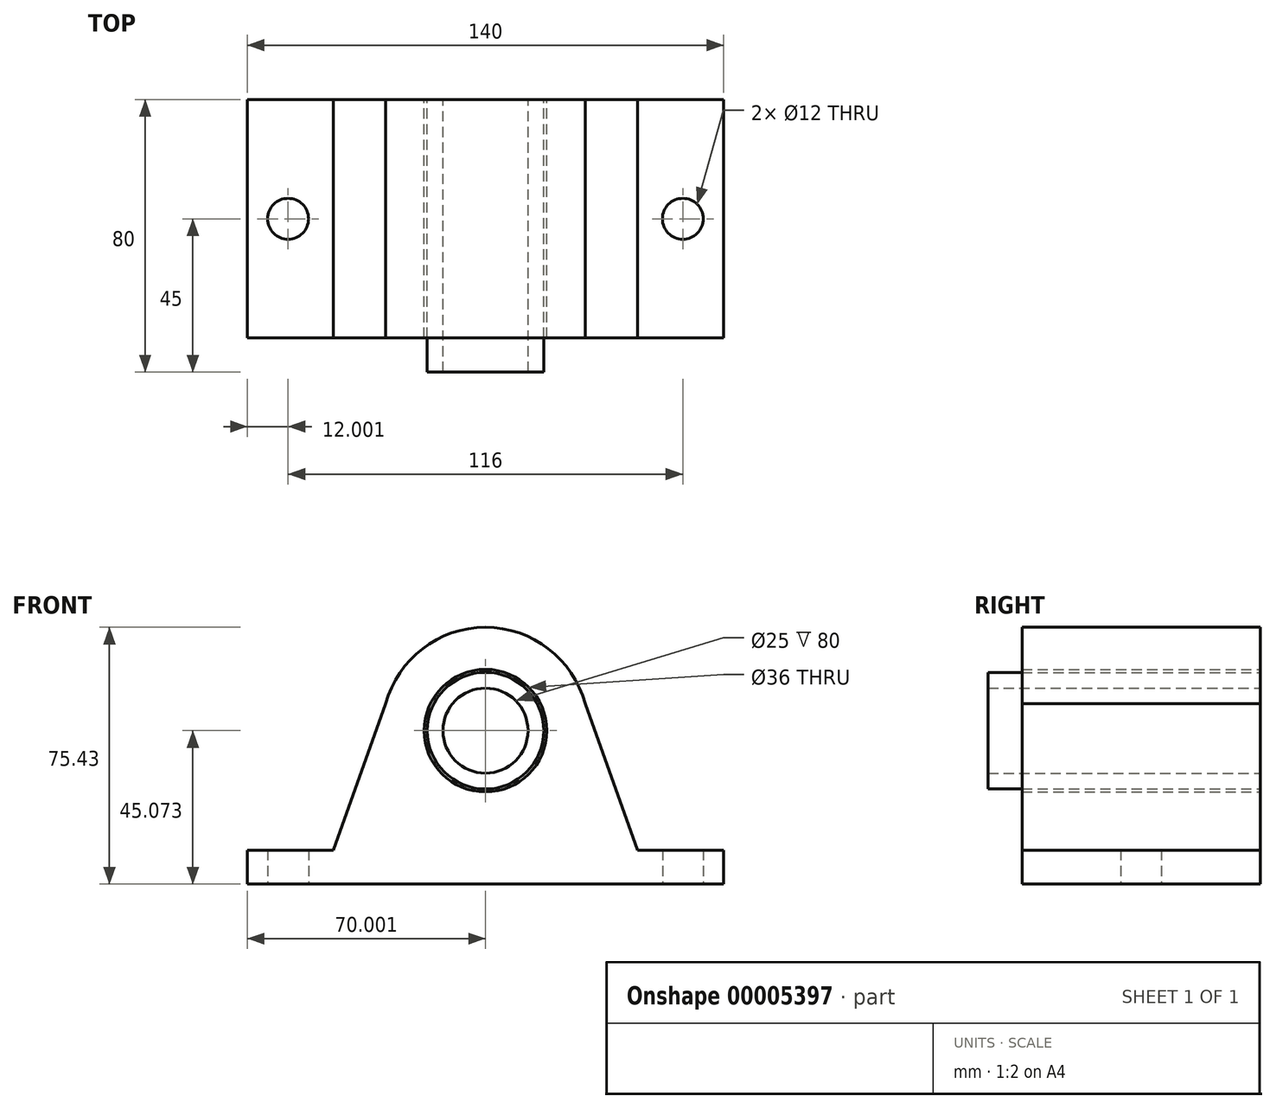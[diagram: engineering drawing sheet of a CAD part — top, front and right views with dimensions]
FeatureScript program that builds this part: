
annotation { "Feature Type Name" : "Feature", "Feature Type Description" : "" }
export const myFeature = defineFeature(function(context is Context, id is Id, definition is map)
    precondition{}
    {
        {
            var Q0;
            Q0=qCreatedBy(makeId("Front.planeOp"),FACE);
            var sketch = newSketch(context, id + "F0", { "sketchPlane" : qUnion([Q0])});
            skCircle(sketch, "E0", {"center": v(-46.77, 40.7) * mm, "radius": 12.5 * mm});
            skCircle(sketch, "E1", {"center": v(-46.77, 40.7) * mm, "radius": 18 * mm});
            skArc(sketch, "E2", {"start": v(-17.46, 48.57) * mm, "mid": v(-46.77, 71.05) * mm, "end": v(-76.08, 48.57) * mm});
            skLineSegment(sketch, "E3", {"start": v(-46.77, 5.62) * mm, "end": v(-116.77, 5.62) * mm});
            skLineSegment(sketch, "E4", {"start": v(-46.77, 5.62) * mm, "end": v(23.23, 5.62) * mm});
            skLineSegment(sketch, "E5.0", {"start": v(-46.77, -4.38) * mm, "end": v(23.23, -4.38) * mm});
            skLineSegment(sketch, "E6.0", {"start": v(-46.77, -4.38) * mm, "end": v(-116.77, -4.38) * mm});
            skLineSegment(sketch, "E7", {"start": v(-116.77, 5.62) * mm, "end": v(-116.77, -4.38) * mm});
            skLineSegment(sketch, "E8", {"start": v(23.23, 5.62) * mm, "end": v(23.23, -4.38) * mm});
            skLineSegment(sketch, "E9", {"start": v(-76.08, 48.57) * mm, "end": v(-91.47, 5.62) * mm});
            skLineSegment(sketch, "E10.0.MirrorCS", {"start": v(-17.46, 48.57) * mm, "end": v(-2.06, 5.62) * mm});
            skSolve(sketch);
        }
        {
            var Q0;
            Q0=makeQuery(id+"F0.imprint","IMPRINT",FACE,{"disambiguationData":[TD([[makeQuery(id+"F0.imprint","IMPRINT",EDGE,{"derivedFrom":sQuery(id+"F0.wireOp",EDGE,"E1")}),-1.0]])]});
            var Q1;
            Q1=makeQuery(id+"F0.imprint","IMPRINT",FACE,{"disambiguationData":[TD([[makeQuery(id+"F0.imprint","IMPRINT",EDGE,{"derivedFrom":sQuery(id+"F0.wireOp",EDGE,"E5.0")}),1.0]])]});
            extrude(context, id + "F1", {"entities" : qUnion([Q0, Q1]), "depth" : 70 * mm});
        }
        {
            var Q0;
            Q0=qCreatedBy(makeId("Front.planeOp"),FACE);
            var sketch = newSketch(context, id + "F2", { "sketchPlane" : qUnion([Q0])});
            skCircle(sketch, "E11.0", {"center": v(-46.77, 40.7) * mm, "radius": 12.5 * mm});
            skCircle(sketch, "E12", {"center": v(-46.77, 40.7) * mm, "radius": 17.12 * mm});
            skSolve(sketch);
        }
        {
            var Q0;
            Q0=makeQuery(id+"F2.imprint","IMPRINT",FACE,{"disambiguationData":[TD([[makeQuery(id+"F2.imprint","IMPRINT",EDGE,{"derivedFrom":sQuery(id+"F2.wireOp",EDGE,"E11.0")}),-1.0]])]});
            extrude(context, id + "F3", {"entities" : qUnion([Q0]), "depth" : 80 * mm});
        }
        {
            var Q0;
            Q0=makeQuery(id+"F1.opExtrude","SWEPT_FACE",FACE,{"disambiguationData":[OSD([sQuery(id+"F0.wireOp",EDGE,"E3")])]});
            var sketch = newSketch(context, id + "F4", { "sketchPlane" : qUnion([Q0])});
            skCircle(sketch, "E13", {"center": v(-104.77, -35) * mm, "radius": 6 * mm});
            skCircle(sketch, "E14", {"center": v(11.23, -35) * mm, "radius": 6 * mm});
            skSolve(sketch);
        }
        {
            var Q0;
            Q0=makeQuery(id+"F4.imprint","IMPRINT",FACE,{"disambiguationData":[TD([[makeQuery(id+"F4.imprint","IMPRINT",EDGE,{"derivedFrom":sQuery(id+"F4.wireOp",EDGE,"E13")}),1.0]])]});
            var Q1;
            Q1=makeQuery(id+"F4.imprint","IMPRINT",FACE,{"disambiguationData":[TD([[makeQuery(id+"F4.imprint","IMPRINT",EDGE,{"derivedFrom":sQuery(id+"F4.wireOp",EDGE,"E14")}),1.0]])]});
            extrude(context, id + "F5", {"entities" : qUnion([Q0, Q1]), "operationType" : NewBodyOperationType.REMOVE, "endBound" : BoundingType.SYMMETRIC, "depth" : 25 * mm});
        }
    });
